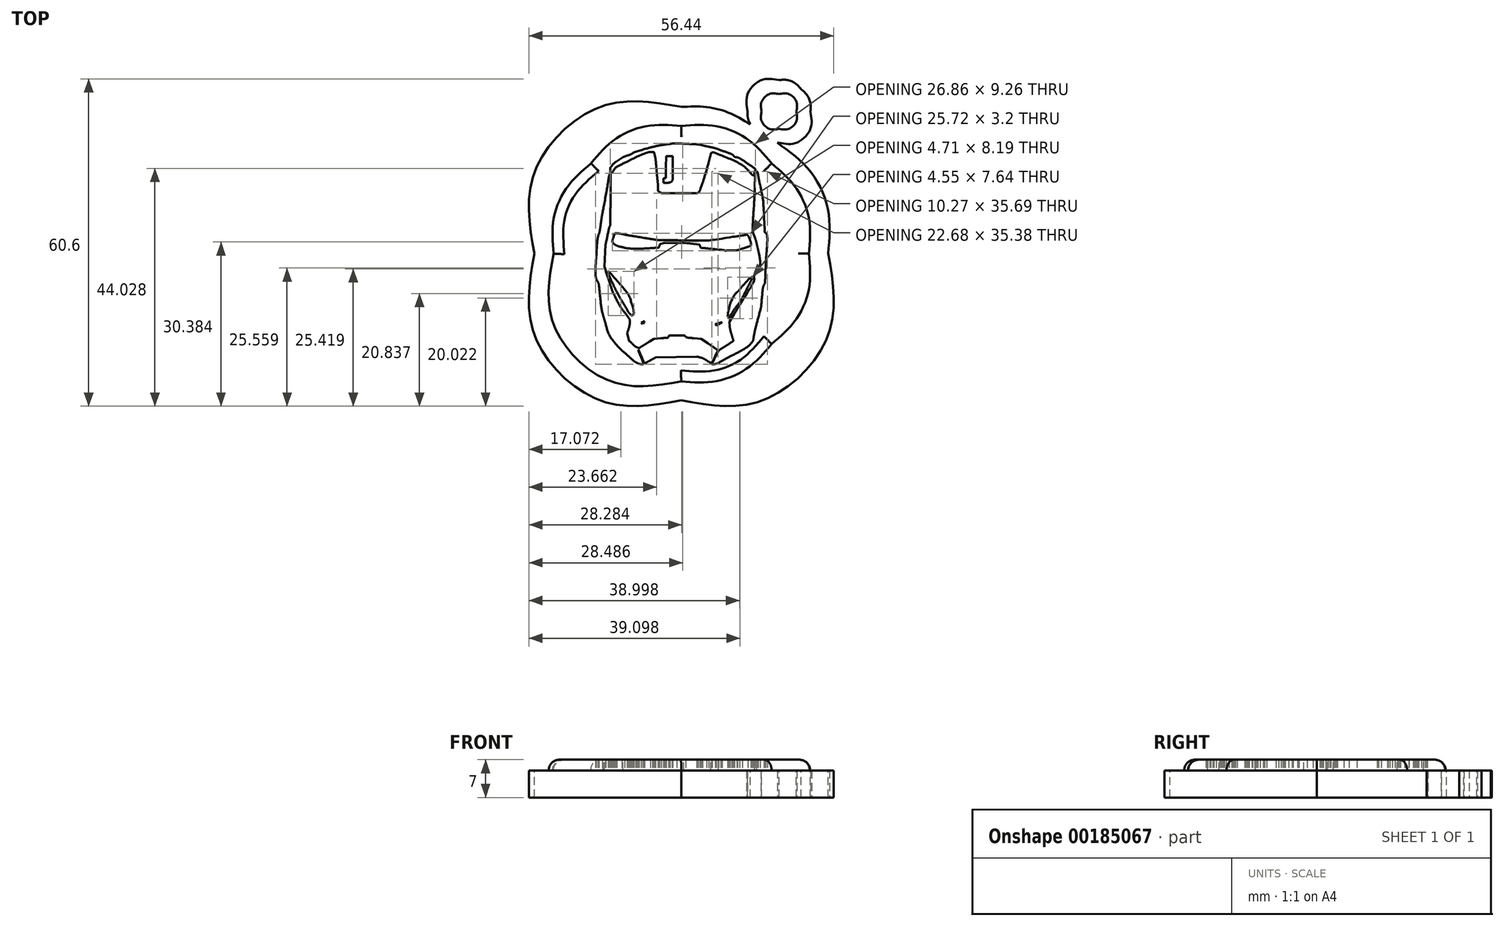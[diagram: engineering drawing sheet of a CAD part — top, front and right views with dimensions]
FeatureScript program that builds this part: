
annotation { "Feature Type Name" : "Feature", "Feature Type Description" : "" }
export const myFeature = defineFeature(function(context is Context, id is Id, definition is map)
    precondition{}
    {
        {
            var Q0;
            Q0=qCreatedBy(makeId("Top.planeOp"),FACE);
            var sketch = newSketch(context, id + "F0", { "sketchPlane" : qUnion([Q0])});
            skFitSpline(sketch, "E0", {"points": [v(-8.22, -22.7) * mm, v(-8.43, -22.6) * mm, v(-8.77, -22.38) * mm, v(-8.96, -22.21) * mm]});
            skFitSpline(sketch, "E1", {"points": [v(-8.96, -22.21) * mm, v(-9.15, -22.04) * mm, v(-9.54, -21.69) * mm, v(-9.83, -21.43) * mm]});
            skFitSpline(sketch, "E2", {"points": [v(-9.83, -21.43) * mm, v(-10.12, -21.17) * mm, v(-10.56, -20.8) * mm, v(-10.8, -20.6) * mm]});
            skFitSpline(sketch, "E3", {"points": [v(-10.8, -20.6) * mm, v(-11.06, -20.39) * mm, v(-11.61, -19.8) * mm, v(-12.04, -19.27) * mm]});
            skFitSpline(sketch, "E4", {"points": [v(-12.04, -19.27) * mm, v(-12.95, -18.16) * mm, v(-13.6, -16.93) * mm, v(-14, -15.53) * mm]});
            skFitSpline(sketch, "E5", {"points": [v(-14, -15.53) * mm, v(-14.14, -15.02) * mm, v(-14.36, -14.26) * mm, v(-14.48, -13.85) * mm]});
            skFitSpline(sketch, "E6", {"points": [v(-14.48, -13.85) * mm, v(-14.7, -13.05) * mm, v(-14.91, -11.53) * mm, v(-15.21, -8.5) * mm]});
            skFitSpline(sketch, "E7", {"points": [v(-15.21, -8.5) * mm, v(-15.23, -8.29) * mm, v(-15.34, -7.94) * mm, v(-15.45, -7.72) * mm]});
            skFitSpline(sketch, "E8", {"points": [v(-15.45, -7.72) * mm, v(-15.78, -7.08) * mm, v(-15.89, -5.4) * mm, v(-15.75, -3.2) * mm]});
            skFitSpline(sketch, "E9", {"points": [v(-15.75, -3.2) * mm, v(-15.59, -0.63) * mm, v(-15.46, 0.49) * mm, v(-15.26, 1.13) * mm]});
            skFitSpline(sketch, "E10", {"points": [v(-15.26, 1.13) * mm, v(-15.16, 1.44) * mm, v(-15, 2.32) * mm, v(-14.9, 3.1) * mm]});
            skFitSpline(sketch, "E11", {"points": [v(-14.9, 3.1) * mm, v(-14.79, 3.87) * mm, v(-14.66, 4.7) * mm, v(-14.6, 4.97) * mm]});
            skFitSpline(sketch, "E12", {"points": [v(-14.6, 4.97) * mm, v(-14.26, 6.74) * mm, v(-13.74, 9.57) * mm, v(-13.58, 10.63) * mm]});
            skFitSpline(sketch, "E13", {"points": [v(-13.58, 10.63) * mm, v(-13.47, 11.32) * mm, v(-13.35, 11.95) * mm, v(-13.32, 12.02) * mm]});
            skFitSpline(sketch, "E14", {"points": [v(-13.32, 12.02) * mm, v(-13.1, 12.44) * mm, v(-13.07, 11.84) * mm, v(-13.1, 7.5) * mm]});
            skFitSpline(sketch, "E15", {"points": [v(-13.1, 7.5) * mm, v(-13.12, 3.82) * mm, v(-13.16, 2.84) * mm, v(-13.27, 2.54) * mm]});
            skFitSpline(sketch, "E16", {"points": [v(-13.27, 2.54) * mm, v(-13.34, 2.33) * mm, v(-13.67, 0.81) * mm, v(-14, -0.83) * mm]});
            skFitSpline(sketch, "E17", {"points": [v(-14.24, -4.9) * mm, v(-14.04, -5.5) * mm, v(-13.61, -6.79) * mm, v(-13.3, -7.76) * mm]});
            skFitSpline(sketch, "E18", {"points": [v(-13.3, -7.76) * mm, v(-12.98, -8.74) * mm, v(-12.6, -9.77) * mm, v(-12.46, -10.06) * mm]});
            skFitSpline(sketch, "E19", {"points": [v(-12.46, -10.06) * mm, v(-11.7, -11.55) * mm, v(-11.06, -12.63) * mm, v(-10.45, -13.43) * mm]});
            skFitSpline(sketch, "E20", {"points": [v(-10.45, -13.43) * mm, v(-10.08, -13.92) * mm, v(-9.73, -14.4) * mm, v(-9.68, -14.5) * mm]});
            skFitSpline(sketch, "E21", {"points": [v(-9.68, -14.5) * mm, v(-9.52, -14.81) * mm, v(-9.71, -16.27) * mm, v(-10.03, -17.2) * mm]});
            skLineSegment(sketch, "E22", {"start": v(-14, -0.83) * mm, "end": v(-14.6, -3.82) * mm});
            skLineSegment(sketch, "E23", {"start": v(-14.6, -3.82) * mm, "end": v(-14.24, -4.9) * mm});
            skLineSegment(sketch, "E24", {"start": v(-14.24, -4.9) * mm, "end": v(-14, -0.83) * mm});
            skFitSpline(sketch, "E25", {"points": [v(-9.63, -18.65) * mm, v(-9.26, -19) * mm, v(-8.73, -19.48) * mm, v(-8.47, -19.74) * mm]});
            skLineSegment(sketch, "E26", {"start": v(-10.03, -17.2) * mm, "end": v(-10.32, -18.03) * mm});
            skLineSegment(sketch, "E27", {"start": v(-10.32, -18.03) * mm, "end": v(-9.63, -18.65) * mm});
            skLineSegment(sketch, "E28", {"start": v(-9.63, -18.65) * mm, "end": v(-10.03, -17.2) * mm});
            skFitSpline(sketch, "E29", {"points": [v(-7.78, -20) * mm, v(-7.66, -19.89) * mm, v(-7.37, -19.68) * mm, v(-7.13, -19.54) * mm]});
            skFitSpline(sketch, "E30", {"points": [v(-7.13, -19.54) * mm, v(-6.9, -19.4) * mm, v(-6.34, -19.06) * mm, v(-5.9, -18.78) * mm]});
            skLineSegment(sketch, "E31", {"start": v(-8.47, -19.74) * mm, "end": v(-8, -20.21) * mm});
            skLineSegment(sketch, "E32", {"start": v(-8, -20.21) * mm, "end": v(-7.78, -20) * mm});
            skLineSegment(sketch, "E33", {"start": v(-7.78, -20) * mm, "end": v(-8.47, -19.74) * mm});
            skFitSpline(sketch, "E34", {"points": [v(-3.8, -18.16) * mm, v(-2.63, -18.07) * mm, v(-2.5, -18.04) * mm, v(-2.37, -17.85) * mm]});
            skFitSpline(sketch, "E35", {"points": [v(-2.37, -17.85) * mm, v(-2.24, -17.65) * mm, v(-2.17, -17.64) * mm, v(-0.82, -17.64) * mm]});
            skFitSpline(sketch, "E36", {"points": [v(-0.82, -17.64) * mm, v(0.48, -17.64) * mm, v(0.6, -17.66) * mm, v(0.8, -17.84) * mm]});
            skFitSpline(sketch, "E37", {"points": [v(0.8, -17.84) * mm, v(0.97, -18) * mm, v(1.21, -18.05) * mm, v(2.35, -18.14) * mm]});
            skLineSegment(sketch, "E38", {"start": v(-5.9, -18.78) * mm, "end": v(-5.11, -18.26) * mm});
            skLineSegment(sketch, "E39", {"start": v(-5.11, -18.26) * mm, "end": v(-3.8, -18.16) * mm});
            skLineSegment(sketch, "E40", {"start": v(-3.8, -18.16) * mm, "end": v(-5.9, -18.78) * mm});
            skFitSpline(sketch, "E41", {"points": [v(4.95, -19.12) * mm, v(5.65, -19.59) * mm, v(6.34, -20.08) * mm, v(6.5, -20.2) * mm]});
            skLineSegment(sketch, "E42", {"start": v(2.35, -18.14) * mm, "end": v(3.7, -18.26) * mm});
            skLineSegment(sketch, "E43", {"start": v(3.7, -18.26) * mm, "end": v(4.95, -19.12) * mm});
            skLineSegment(sketch, "E44", {"start": v(4.95, -19.12) * mm, "end": v(2.35, -18.14) * mm});
            skFitSpline(sketch, "E45", {"points": [v(6.24, -21.52) * mm, v(5.94, -22.12) * mm, v(5.63, -22.63) * mm, v(5.56, -22.66) * mm]});
            skFitSpline(sketch, "E46", {"points": [v(5.56, -22.66) * mm, v(5.49, -22.7) * mm, v(5.1, -22.51) * mm, v(4.7, -22.27) * mm]});
            skFitSpline(sketch, "E47", {"points": [v(4.7, -22.27) * mm, v(4.13, -21.93) * mm, v(3.73, -21.77) * mm, v(2.85, -21.55) * mm]});
            skLineSegment(sketch, "E48", {"start": v(6.5, -20.2) * mm, "end": v(6.78, -20.43) * mm});
            skLineSegment(sketch, "E49", {"start": v(6.78, -20.43) * mm, "end": v(6.24, -21.52) * mm});
            skLineSegment(sketch, "E50", {"start": v(6.24, -21.52) * mm, "end": v(6.5, -20.2) * mm});
            skFitSpline(sketch, "E51", {"points": [v(-4.73, -21.7) * mm, v(-5.04, -21.87) * mm, v(-5.61, -22.18) * mm, v(-6, -22.4) * mm]});
            skFitSpline(sketch, "E52", {"points": [v(-6, -22.4) * mm, v(-6.38, -22.6) * mm, v(-6.74, -22.75) * mm, v(-6.8, -22.71) * mm]});
            skFitSpline(sketch, "E53", {"points": [v(-6.8, -22.71) * mm, v(-6.85, -22.68) * mm, v(-7, -22.42) * mm, v(-7.11, -22.13) * mm]});
            skFitSpline(sketch, "E54", {"points": [v(-7.11, -22.13) * mm, v(-7.53, -21.14) * mm, v(-7.9, -20.35) * mm, v(-7.93, -20.39) * mm]});
            skFitSpline(sketch, "E55", {"points": [v(-7.93, -20.39) * mm, v(-7.95, -20.4) * mm, v(-7.76, -20.94) * mm, v(-7.5, -21.57) * mm]});
            skFitSpline(sketch, "E56", {"points": [v(-7.5, -21.57) * mm, v(-7.24, -22.2) * mm, v(-7.03, -22.76) * mm, v(-7.03, -22.8) * mm]});
            skFitSpline(sketch, "E57", {"points": [v(-7.03, -22.8) * mm, v(-7.03, -22.95) * mm, v(-7.81, -22.88) * mm, v(-8.22, -22.7) * mm]});
            skLineSegment(sketch, "E58", {"start": v(2.85, -21.55) * mm, "end": v(1.73, -21.27) * mm});
            skLineSegment(sketch, "E59", {"start": v(1.73, -21.27) * mm, "end": v(-1.22, -21.34) * mm});
            skLineSegment(sketch, "E60", {"start": v(-1.22, -21.34) * mm, "end": v(-4.17, -21.4) * mm});
            skLineSegment(sketch, "E61", {"start": v(-4.17, -21.4) * mm, "end": v(-4.73, -21.7) * mm});
            skLineSegment(sketch, "E62", {"start": v(-4.73, -21.7) * mm, "end": v(2.85, -21.55) * mm});
            skFitSpline(sketch, "E63", {"points": [v(5.72, -22.81) * mm, v(5.88, -22.45) * mm, v(6.87, -20.56) * mm, v(6.95, -20.44) * mm]});
            skFitSpline(sketch, "E64", {"points": [v(6.95, -20.44) * mm, v(7.01, -20.37) * mm, v(7.59, -19.97) * mm, v(8.23, -19.56) * mm]});
            skFitSpline(sketch, "E65", {"points": [v(8.23, -19.56) * mm, v(8.87, -19.16) * mm, v(9.46, -18.77) * mm, v(9.52, -18.71) * mm]});
            skFitSpline(sketch, "E66", {"points": [v(9.52, -18.71) * mm, v(9.63, -18.62) * mm, v(9.6, -18.41) * mm, v(9.33, -17.54) * mm]});
            skFitSpline(sketch, "E67", {"points": [v(9.33, -17.54) * mm, v(9.15, -16.95) * mm, v(8.98, -16.17) * mm, v(8.95, -15.8) * mm]});
            skFitSpline(sketch, "E68", {"points": [v(9.78, -13.67) * mm, v(10.27, -12.85) * mm, v(11, -11.68) * mm, v(11.39, -11.05) * mm]});
            skFitSpline(sketch, "E69", {"points": [v(11.39, -11.05) * mm, v(12.53, -9.23) * mm, v(13.47, -7.38) * mm, v(13.47, -6.95) * mm]});
            skFitSpline(sketch, "E70", {"points": [v(13.47, -6.95) * mm, v(13.47, -6.67) * mm, v(13.61, -6.33) * mm, v(14.03, -5.57) * mm]});
            skFitSpline(sketch, "E71", {"points": [v(14.03, -5.57) * mm, v(14.42, -4.87) * mm, v(14.6, -4.46) * mm, v(14.6, -4.23) * mm]});
            skFitSpline(sketch, "E72", {"points": [v(14.6, -4.23) * mm, v(14.6, -3.9) * mm, v(14.38, -2.52) * mm, v(14.23, -1.87) * mm]});
            skFitSpline(sketch, "E73", {"points": [v(14.23, -1.87) * mm, v(14.18, -1.66) * mm, v(14.07, -1.18) * mm, v(13.98, -0.8) * mm]});
            skFitSpline(sketch, "E74", {"points": [v(13.98, -0.8) * mm, v(13.9, -0.4) * mm, v(13.72, 0.2) * mm, v(13.6, 0.57) * mm]});
            skFitSpline(sketch, "E75", {"points": [v(13.6, 0.57) * mm, v(13.27, 1.49) * mm, v(13.23, 2.84) * mm, v(13.43, 6.28) * mm]});
            skFitSpline(sketch, "E76", {"points": [v(13.43, 6.28) * mm, v(13.52, 7.82) * mm, v(13.6, 9.76) * mm, v(13.62, 10.58) * mm]});
            skFitSpline(sketch, "E77", {"points": [v(13.62, 10.58) * mm, v(13.64, 12.14) * mm, v(13.72, 12.62) * mm, v(13.95, 12.67) * mm]});
            skFitSpline(sketch, "E78", {"points": [v(13.95, 12.67) * mm, v(14.06, 12.69) * mm, v(14.2, 12.19) * mm, v(14.58, 10.23) * mm]});
            skFitSpline(sketch, "E79", {"points": [v(14.58, 10.23) * mm, v(15.08, 7.68) * mm, v(15.18, 6.84) * mm, v(15.35, 3.47) * mm]});
            skFitSpline(sketch, "E80", {"points": [v(15.35, 3.47) * mm, v(15.43, 1.84) * mm, v(15.47, 1.48) * mm, v(15.6, 1.33) * mm]});
            skFitSpline(sketch, "E81", {"points": [v(15.6, 1.33) * mm, v(15.82, 1.1) * mm, v(15.87, -0.9) * mm, v(15.72, -3) * mm]});
            skFitSpline(sketch, "E82", {"points": [v(15.72, -3) * mm, v(15.66, -3.81) * mm, v(15.6, -5.25) * mm, v(15.56, -6.17) * mm]});
            skFitSpline(sketch, "E83", {"points": [v(15.56, -6.17) * mm, v(15.51, -7.63) * mm, v(15.48, -7.91) * mm, v(15.3, -8.32) * mm]});
            skFitSpline(sketch, "E84", {"points": [v(15.3, -8.32) * mm, v(15.14, -8.69) * mm, v(15.05, -9.2) * mm, v(14.93, -10.53) * mm]});
            skFitSpline(sketch, "E85", {"points": [v(14.93, -10.53) * mm, v(14.77, -12.27) * mm, v(14.72, -12.52) * mm, v(14.27, -14.22) * mm]});
            skFitSpline(sketch, "E86", {"points": [v(14.27, -14.22) * mm, v(13.86, -15.73) * mm, v(13.58, -16.96) * mm, v(13.37, -18.1) * mm]});
            skFitSpline(sketch, "E87", {"points": [v(13.37, -18.1) * mm, v(13.29, -18.53) * mm, v(13.18, -18.79) * mm, v(12.98, -19.01) * mm]});
            skFitSpline(sketch, "E88", {"points": [v(12.98, -19.01) * mm, v(12.59, -19.46) * mm, v(11.16, -20.41) * mm, v(9.85, -21.1) * mm]});
            skFitSpline(sketch, "E89", {"points": [v(9.85, -21.1) * mm, v(9.24, -21.43) * mm, v(8.4, -21.87) * mm, v(8, -22.09) * mm]});
            skFitSpline(sketch, "E90", {"points": [v(8, -22.09) * mm, v(7.59, -22.3) * mm, v(7.08, -22.58) * mm, v(6.88, -22.69) * mm]});
            skFitSpline(sketch, "E91", {"points": [v(6.88, -22.69) * mm, v(6.52, -22.87) * mm, v(5.65, -22.97) * mm, v(5.72, -22.81) * mm]});
            skLineSegment(sketch, "E92", {"start": v(8.95, -15.8) * mm, "end": v(8.89, -15.14) * mm});
            skLineSegment(sketch, "E93", {"start": v(8.89, -15.14) * mm, "end": v(9.78, -13.67) * mm});
            skLineSegment(sketch, "E94", {"start": v(9.78, -13.67) * mm, "end": v(8.95, -15.8) * mm});
            skFitSpline(sketch, "E95", {"points": [v(5.7, -16.17) * mm, v(5.41, -15.87) * mm, v(5.07, -15.49) * mm, v(4.93, -15.31) * mm]});
            skFitSpline(sketch, "E96", {"points": [v(4.93, -15.31) * mm, v(4.77, -15.12) * mm, v(4.53, -14.96) * mm, v(4.32, -14.91) * mm]});
            skFitSpline(sketch, "E97", {"points": [v(4.32, -14.91) * mm, v(3.86, -14.8) * mm, v(-4.6, -14.64) * mm, v(-5.04, -14.74) * mm]});
            skFitSpline(sketch, "E98", {"points": [v(-5.04, -14.74) * mm, v(-5.31, -14.8) * mm, v(-5.55, -15) * mm, v(-6.17, -15.67) * mm]});
            skFitSpline(sketch, "E99", {"points": [v(-6.17, -15.67) * mm, v(-6.6, -16.14) * mm, v(-7.02, -16.52) * mm, v(-7.1, -16.52) * mm]});
            skFitSpline(sketch, "E100", {"points": [v(-7.1, -16.52) * mm, v(-7.2, -16.52) * mm, v(-7.6, -16.24) * mm, v(-8.01, -15.9) * mm]});
            skFitSpline(sketch, "E101", {"points": [v(-8.01, -15.9) * mm, v(-9.43, -14.71) * mm, v(-9.39, -14.76) * mm, v(-9.32, -14.45) * mm]});
            skFitSpline(sketch, "E102", {"points": [v(-9.32, -14.45) * mm, v(-9.28, -14.3) * mm, v(-9.2, -14.14) * mm, v(-9.12, -14.11) * mm]});
            skFitSpline(sketch, "E103", {"points": [v(-9.12, -14.11) * mm, v(-9.05, -14.08) * mm, v(-8.72, -14.28) * mm, v(-8.36, -14.57) * mm]});
            skFitSpline(sketch, "E104", {"points": [v(-8.36, -14.57) * mm, v(-8.01, -14.85) * mm, v(-7.6, -15.17) * mm, v(-7.43, -15.28) * mm]});
            skFitSpline(sketch, "E105", {"points": [v(-6.77, -15) * mm, v(-6.57, -14.73) * mm, v(-6.34, -14.39) * mm, v(-6.25, -14.25) * mm]});
            skFitSpline(sketch, "E106", {"points": [v(-6.25, -14.25) * mm, v(-5.88, -13.66) * mm, v(-6.02, -13.68) * mm, v(-1.47, -13.7) * mm]});
            skFitSpline(sketch, "E107", {"points": [v(-1.47, -13.7) * mm, v(2.96, -13.7) * mm, v(4.58, -13.76) * mm, v(4.95, -13.9) * mm]});
            skFitSpline(sketch, "E108", {"points": [v(4.95, -13.9) * mm, v(5.08, -13.96) * mm, v(5.39, -14.28) * mm, v(5.63, -14.63) * mm]});
            skFitSpline(sketch, "E109", {"points": [v(5.63, -14.63) * mm, v(5.88, -14.97) * mm, v(6.17, -15.37) * mm, v(6.29, -15.51) * mm]});
            skLineSegment(sketch, "E110", {"start": v(-7.43, -15.28) * mm, "end": v(-7.13, -15.5) * mm});
            skLineSegment(sketch, "E111", {"start": v(-7.13, -15.5) * mm, "end": v(-6.77, -15) * mm});
            skLineSegment(sketch, "E112", {"start": v(-6.77, -15) * mm, "end": v(-7.43, -15.28) * mm});
            skFitSpline(sketch, "E113", {"points": [v(7.53, -15.16) * mm, v(8.1, -14.83) * mm, v(8.61, -14.55) * mm, v(8.68, -14.55) * mm]});
            skFitSpline(sketch, "E114", {"points": [v(8.68, -14.55) * mm, v(8.76, -14.55) * mm, v(8.8, -14.65) * mm, v(8.78, -14.85) * mm]});
            skFitSpline(sketch, "E115", {"points": [v(8.78, -14.85) * mm, v(8.75, -15.1) * mm, v(8.62, -15.23) * mm, v(7.63, -15.92) * mm]});
            skFitSpline(sketch, "E116", {"points": [v(7.63, -15.92) * mm, v(7.01, -16.35) * mm, v(6.44, -16.7) * mm, v(6.35, -16.7) * mm]});
            skFitSpline(sketch, "E117", {"points": [v(6.35, -16.7) * mm, v(6.27, -16.7) * mm, v(5.97, -16.46) * mm, v(5.7, -16.17) * mm]});
            skLineSegment(sketch, "E118", {"start": v(6.29, -15.51) * mm, "end": v(6.5, -15.77) * mm});
            skLineSegment(sketch, "E119", {"start": v(6.5, -15.77) * mm, "end": v(7.53, -15.16) * mm});
            skLineSegment(sketch, "E120", {"start": v(7.53, -15.16) * mm, "end": v(6.29, -15.51) * mm});
            skFitSpline(sketch, "E121", {"points": [v(8.72, -14.34) * mm, v(8.62, -14.21) * mm, v(8.72, -13.1) * mm, v(8.9, -12.4) * mm]});
            skFitSpline(sketch, "E122", {"points": [v(8.9, -12.4) * mm, v(9.1, -11.62) * mm, v(10.02, -9.88) * mm, v(10.42, -9.54) * mm]});
            skFitSpline(sketch, "E123", {"points": [v(10.42, -9.54) * mm, v(10.48, -9.5) * mm, v(10.65, -9.3) * mm, v(10.8, -9.12) * mm]});
            skFitSpline(sketch, "E124", {"points": [v(10.8, -9.12) * mm, v(11.44, -8.33) * mm, v(12.94, -6.87) * mm, v(13.06, -6.91) * mm]});
            skFitSpline(sketch, "E125", {"points": [v(13.06, -6.91) * mm, v(13.15, -6.95) * mm, v(13.03, -7.25) * mm, v(12.62, -8.06) * mm]});
            skFitSpline(sketch, "E126", {"points": [v(12.62, -8.06) * mm, v(11.48, -10.26) * mm, v(10.72, -11.61) * mm, v(10.34, -12.12) * mm]});
            skFitSpline(sketch, "E127", {"points": [v(10.34, -12.12) * mm, v(9.88, -12.72) * mm, v(8.98, -14.2) * mm, v(8.98, -14.35) * mm]});
            skFitSpline(sketch, "E128", {"points": [v(8.98, -14.35) * mm, v(8.98, -14.5) * mm, v(8.84, -14.49) * mm, v(8.72, -14.34) * mm]});
            skFitSpline(sketch, "E129", {"points": [v(-9.47, -13.68) * mm, v(-9.64, -13.5) * mm, v(-9.87, -13.2) * mm, v(-9.97, -13) * mm]});
            skFitSpline(sketch, "E130", {"points": [v(-9.97, -13) * mm, v(-10.07, -12.8) * mm, v(-10.53, -12) * mm, v(-11, -11.23) * mm]});
            skFitSpline(sketch, "E131", {"points": [v(-11, -11.23) * mm, v(-11.46, -10.46) * mm, v(-12.05, -9.36) * mm, v(-12.33, -8.8) * mm]});
            skFitSpline(sketch, "E132", {"points": [v(-12.33, -8.8) * mm, v(-12.83, -7.74) * mm, v(-13.49, -6.17) * mm, v(-13.49, -6.01) * mm]});
            skFitSpline(sketch, "E133", {"points": [v(-13.49, -6.01) * mm, v(-13.49, -5.78) * mm, v(-13.14, -6.08) * mm, v(-12.3, -7.06) * mm]});
            skFitSpline(sketch, "E134", {"points": [v(-12.3, -7.06) * mm, v(-10.33, -9.34) * mm, v(-9.62, -10.41) * mm, v(-9.18, -11.74) * mm]});
            skFitSpline(sketch, "E135", {"points": [v(-9.18, -11.74) * mm, v(-8.92, -12.56) * mm, v(-8.82, -13.72) * mm, v(-9.01, -13.87) * mm]});
            skFitSpline(sketch, "E136", {"points": [v(-9.01, -13.87) * mm, v(-9.13, -13.97) * mm, v(-9.2, -13.93) * mm, v(-9.47, -13.68) * mm]});
            skFitSpline(sketch, "E137", {"points": [v(7.95, -1.88) * mm, v(7.92, -1.86) * mm, v(7.02, -1.75) * mm, v(5.94, -1.64) * mm]});
            skFitSpline(sketch, "E138", {"points": [v(5.94, -1.64) * mm, v(3.79, -1.42) * mm, v(3.58, -1.35) * mm, v(3.41, -0.8) * mm]});
            skFitSpline(sketch, "E139", {"points": [v(0.42, -0.5) * mm, v(-1.18, -0.49) * mm, v(-2.8, -0.47) * mm, v(-3.18, -0.47) * mm]});
            skLineSegment(sketch, "E140", {"start": v(3.41, -0.8) * mm, "end": v(3.32, -0.51) * mm});
            skLineSegment(sketch, "E141", {"start": v(3.32, -0.51) * mm, "end": v(0.42, -0.5) * mm});
            skLineSegment(sketch, "E142", {"start": v(0.42, -0.5) * mm, "end": v(3.41, -0.8) * mm});
            skFitSpline(sketch, "E143", {"points": [v(-3.98, -0.76) * mm, v(-4.17, -1.33) * mm, v(-4.27, -1.37) * mm, v(-5.73, -1.46) * mm]});
            skFitSpline(sketch, "E144", {"points": [v(-5.73, -1.46) * mm, v(-7.53, -1.57) * mm, v(-10.06, -1.47) * mm, v(-10.98, -1.26) * mm]});
            skFitSpline(sketch, "E145", {"points": [v(-10.98, -1.26) * mm, v(-11.64, -1.11) * mm, v(-12.47, -0.7) * mm, v(-12.72, -0.39) * mm]});
            skFitSpline(sketch, "E146", {"points": [v(-12.72, -0.39) * mm, v(-12.79, -0.3) * mm, v(-12.74, -0.04) * mm, v(-12.57, 0.5) * mm]});
            skLineSegment(sketch, "E147", {"start": v(-3.18, -0.47) * mm, "end": v(-3.87, -0.46) * mm});
            skLineSegment(sketch, "E148", {"start": v(-3.87, -0.46) * mm, "end": v(-3.98, -0.76) * mm});
            skLineSegment(sketch, "E149", {"start": v(-3.98, -0.76) * mm, "end": v(-3.18, -0.47) * mm});
            skFitSpline(sketch, "E150", {"points": [v(-11.92, 1.27) * mm, v(-11.7, 1.27) * mm, v(-11.13, 1.19) * mm, v(-10.65, 1.09) * mm]});
            skFitSpline(sketch, "E151", {"points": [v(-10.65, 1.09) * mm, v(-9.79, 0.9) * mm, v(-9.34, 0.83) * mm, v(-6.51, 0.38) * mm]});
            skFitSpline(sketch, "E152", {"points": [v(-6.51, 0.38) * mm, v(-5.69, 0.24) * mm, v(-4.9, 0.11) * mm, v(-4.78, 0.09) * mm]});
            skFitSpline(sketch, "E153", {"points": [v(-4.78, 0.09) * mm, v(-4.65, 0.06) * mm, v(-2.78, 0.02) * mm, v(-0.63, -0.01) * mm]});
            skFitSpline(sketch, "E154", {"points": [v(-0.63, -0.01) * mm, v(3.84, -0.08) * mm, v(5.67, 0.04) * mm, v(9.5, 0.62) * mm]});
            skFitSpline(sketch, "E155", {"points": [v(9.5, 0.62) * mm, v(12, 1) * mm, v(12.17, 1.02) * mm, v(12.3, 0.88) * mm]});
            skFitSpline(sketch, "E156", {"points": [v(12.3, 0.88) * mm, v(12.41, 0.77) * mm, v(12.91, -0.62) * mm, v(12.91, -0.81) * mm]});
            skFitSpline(sketch, "E157", {"points": [v(12.91, -0.81) * mm, v(12.91, -0.93) * mm, v(12.19, -1.26) * mm, v(11.28, -1.57) * mm]});
            skFitSpline(sketch, "E158", {"points": [v(11.28, -1.57) * mm, v(10.55, -1.8) * mm, v(10.26, -1.86) * mm, v(9.21, -1.9) * mm]});
            skFitSpline(sketch, "E159", {"points": [v(9.21, -1.9) * mm, v(8.54, -1.91) * mm, v(7.98, -1.9) * mm, v(7.95, -1.88) * mm]});
            skLineSegment(sketch, "E160", {"start": v(-12.57, 0.5) * mm, "end": v(-12.32, 1.27) * mm});
            skLineSegment(sketch, "E161", {"start": v(-12.32, 1.27) * mm, "end": v(-11.92, 1.27) * mm});
            skLineSegment(sketch, "E162", {"start": v(-11.92, 1.27) * mm, "end": v(-12.57, 0.5) * mm});
            skFitSpline(sketch, "E163", {"points": [v(-3.66, 8.74) * mm, v(-3.73, 8.76) * mm, v(-3.91, 8.86) * mm, v(-4.05, 8.96) * mm]});
            skFitSpline(sketch, "E164", {"points": [v(-4.05, 8.96) * mm, v(-4.29, 9.13) * mm, v(-4.31, 9.2) * mm, v(-4.31, 9.7) * mm]});
            skFitSpline(sketch, "E165", {"points": [v(-4.31, 9.7) * mm, v(-4.31, 10.02) * mm, v(-4.35, 10.66) * mm, v(-4.4, 11.13) * mm]});
            skFitSpline(sketch, "E166", {"points": [v(-4.4, 11.13) * mm, v(-4.45, 11.6) * mm, v(-4.54, 12.51) * mm, v(-4.6, 13.16) * mm]});
            skFitSpline(sketch, "E167", {"points": [v(-4.6, 13.16) * mm, v(-4.72, 14.56) * mm, v(-4.85, 15.51) * mm, v(-4.97, 15.99) * mm]});
            skFitSpline(sketch, "E168", {"points": [v(-4.97, 15.99) * mm, v(-5.06, 16.3) * mm, v(-5.1, 16.34) * mm, v(-5.34, 16.34) * mm]});
            skFitSpline(sketch, "E169", {"points": [v(-5.34, 16.34) * mm, v(-5.88, 16.34) * mm, v(-8.3, 15.43) * mm, v(-9.97, 14.59) * mm]});
            skFitSpline(sketch, "E170", {"points": [v(-9.97, 14.59) * mm, v(-11.42, 13.87) * mm, v(-12.25, 13.33) * mm, v(-12.5, 12.96) * mm]});
            skFitSpline(sketch, "E171", {"points": [v(-12.5, 12.96) * mm, v(-12.85, 12.46) * mm, v(-13.08, 12.47) * mm, v(-13.13, 13) * mm]});
            skFitSpline(sketch, "E172", {"points": [v(-13.13, 13) * mm, v(-13.16, 13.34) * mm, v(-13.13, 13.44) * mm, v(-12.84, 13.8) * mm]});
            skFitSpline(sketch, "E173", {"points": [v(-12.84, 13.8) * mm, v(-12.46, 14.25) * mm, v(-10.5, 15.5) * mm, v(-9.78, 15.75) * mm]});
            skFitSpline(sketch, "E174", {"points": [v(-9.78, 15.75) * mm, v(-9.53, 15.83) * mm, v(-9.24, 15.95) * mm, v(-9.13, 16.02) * mm]});
            skFitSpline(sketch, "E175", {"points": [v(-9.13, 16.02) * mm, v(-8.86, 16.19) * mm, v(-6.54, 16.95) * mm, v(-5.32, 17.26) * mm]});
            skFitSpline(sketch, "E176", {"points": [v(-5.32, 17.26) * mm, v(-4.74, 17.42) * mm, v(-3.6, 17.63) * mm, v(-2.77, 17.74) * mm]});
            skFitSpline(sketch, "E177", {"points": [v(-2.77, 17.74) * mm, v(-1.37, 17.94) * mm, v(-1.12, 17.94) * mm, v(0.93, 17.85) * mm]});
            skFitSpline(sketch, "E178", {"points": [v(0.93, 17.85) * mm, v(2.5, 17.79) * mm, v(3.36, 17.7) * mm, v(3.93, 17.58) * mm]});
            skFitSpline(sketch, "E179", {"points": [v(3.93, 17.58) * mm, v(4.36, 17.47) * mm, v(5.06, 17.32) * mm, v(5.47, 17.23) * mm]});
            skFitSpline(sketch, "E180", {"points": [v(5.47, 17.23) * mm, v(5.88, 17.14) * mm, v(6.5, 16.97) * mm, v(6.83, 16.85) * mm]});
            skFitSpline(sketch, "E181", {"points": [v(6.83, 16.85) * mm, v(8.6, 16.21) * mm, v(9.51, 15.82) * mm, v(9.68, 15.63) * mm]});
            skFitSpline(sketch, "E182", {"points": [v(9.68, 15.63) * mm, v(9.8, 15.5) * mm, v(10.03, 15.4) * mm, v(10.26, 15.36) * mm]});
            skFitSpline(sketch, "E183", {"points": [v(10.26, 15.36) * mm, v(10.53, 15.31) * mm, v(11.01, 15.05) * mm, v(11.85, 14.48) * mm]});
            skFitSpline(sketch, "E184", {"points": [v(11.85, 14.48) * mm, v(13.28, 13.52) * mm, v(13.7, 13.13) * mm, v(13.62, 12.84) * mm]});
            skFitSpline(sketch, "E185", {"points": [v(13.62, 12.84) * mm, v(13.59, 12.73) * mm, v(13.54, 12.53) * mm, v(13.5, 12.38) * mm]});
            skFitSpline(sketch, "E186", {"points": [v(13.5, 12.38) * mm, v(13.42, 12.01) * mm, v(13.2, 12.06) * mm, v(12.72, 12.56) * mm]});
            skFitSpline(sketch, "E187", {"points": [v(12.72, 12.56) * mm, v(11.7, 13.6) * mm, v(9.84, 14.7) * mm, v(7.3, 15.74) * mm]});
            skFitSpline(sketch, "E188", {"points": [v(7.3, 15.74) * mm, v(6.23, 16.17) * mm, v(5.81, 16.3) * mm, v(5.7, 16.24) * mm]});
            skFitSpline(sketch, "E189", {"points": [v(5.7, 16.24) * mm, v(5.51, 16.14) * mm, v(5.45, 15.96) * mm, v(5.1, 14.56) * mm]});
            skFitSpline(sketch, "E190", {"points": [v(5.1, 14.56) * mm, v(4.86, 13.61) * mm, v(3.93, 10.6) * mm, v(3.53, 9.48) * mm]});
            skFitSpline(sketch, "E191", {"points": [v(3.53, 9.48) * mm, v(3.42, 9.17) * mm, v(3.25, 8.89) * mm, v(3.14, 8.82) * mm]});
            skFitSpline(sketch, "E192", {"points": [v(3.14, 8.82) * mm, v(3, 8.74) * mm, v(2.04, 8.7) * mm, v(-0.29, 8.7) * mm]});
            skFitSpline(sketch, "E193", {"points": [v(-0.29, 8.7) * mm, v(-2.06, 8.7) * mm, v(-3.58, 8.71) * mm, v(-3.66, 8.74) * mm]});
            skFitSpline(sketch, "E194", {"points": [v(-2.08, 10.73) * mm, v(-1.91, 10.79) * mm, v(-1.74, 10.91) * mm, v(-1.69, 11) * mm]});
            skFitSpline(sketch, "E195", {"points": [v(-1.69, 11) * mm, v(-1.64, 11.1) * mm, v(-1.6, 12.12) * mm, v(-1.6, 13.38) * mm]});
            skFitSpline(sketch, "E196", {"points": [v(-2.84, 13.55) * mm, v(-2.86, 11.52) * mm, v(-2.86, 11.52) * mm, v(-3.07, 11.49) * mm]});
            skFitSpline(sketch, "E197", {"points": [v(-3.07, 11.49) * mm, v(-3.25, 11.46) * mm, v(-3.28, 11.4) * mm, v(-3.28, 11.04) * mm]});
            skLineSegment(sketch, "E198", {"start": v(-1.6, 13.38) * mm, "end": v(-1.6, 15.59) * mm});
            skLineSegment(sketch, "E199", {"start": v(-1.6, 15.59) * mm, "end": v(-2.2, 15.59) * mm});
            skLineSegment(sketch, "E200", {"start": v(-2.2, 15.59) * mm, "end": v(-2.81, 15.59) * mm});
            skLineSegment(sketch, "E201", {"start": v(-2.81, 15.59) * mm, "end": v(-2.84, 13.55) * mm});
            skFitSpline(sketch, "E202", {"points": [v(-2.83, 10.63) * mm, v(-2.58, 10.63) * mm, v(-2.24, 10.68) * mm, v(-2.08, 10.73) * mm]});
            skLineSegment(sketch, "E203", {"start": v(-3.28, 11.04) * mm, "end": v(-3.28, 10.63) * mm});
            skLineSegment(sketch, "E204", {"start": v(-3.28, 10.63) * mm, "end": v(-2.83, 10.63) * mm});
            skFitSpline(sketch, "E205", {"points": [v(0.1, 12.3) * mm, v(0.11, 13.95) * mm, v(0.11, 13.95) * mm, v(0.23, 13.25) * mm]});
            skFitSpline(sketch, "E206", {"points": [v(0.23, 13.25) * mm, v(0.3, 12.86) * mm, v(0.4, 12.12) * mm, v(0.46, 11.59) * mm]});
            skFitSpline(sketch, "E207", {"points": [v(0.94, 10.63) * mm, v(1.14, 10.63) * mm, v(1.3, 10.66) * mm, v(1.3, 10.7) * mm]});
            skFitSpline(sketch, "E208", {"points": [v(1.3, 10.7) * mm, v(1.3, 10.87) * mm, v(1.69, 13.77) * mm, v(1.72, 13.86) * mm]});
            skFitSpline(sketch, "E209", {"points": [v(1.72, 13.86) * mm, v(1.74, 13.9) * mm, v(1.76, 13.36) * mm, v(1.77, 12.64) * mm]});
            skFitSpline(sketch, "E210", {"points": [v(1.77, 12.64) * mm, v(1.77, 11.92) * mm, v(1.8, 11.17) * mm, v(1.83, 10.98) * mm]});
            skLineSegment(sketch, "E211", {"start": v(0.46, 11.59) * mm, "end": v(0.58, 10.63) * mm});
            skLineSegment(sketch, "E212", {"start": v(0.58, 10.63) * mm, "end": v(0.94, 10.63) * mm});
            skFitSpline(sketch, "E213", {"points": [v(2.11, 15.59) * mm, v(1.2, 15.59) * mm, v(1.3, 15.71) * mm, v(1.11, 14.25) * mm]});
            skFitSpline(sketch, "E214", {"points": [v(1.11, 14.25) * mm, v(1.05, 13.74) * mm, v(0.97, 13.36) * mm, v(0.93, 13.4) * mm]});
            skFitSpline(sketch, "E215", {"points": [v(0.93, 13.4) * mm, v(0.9, 13.45) * mm, v(0.81, 13.86) * mm, v(0.75, 14.33) * mm]});
            skFitSpline(sketch, "E216", {"points": [v(0.75, 14.33) * mm, v(0.56, 15.71) * mm, v(0.65, 15.59) * mm, v(-0.25, 15.59) * mm]});
            skLineSegment(sketch, "E217", {"start": v(1.83, 10.98) * mm, "end": v(1.9, 10.63) * mm});
            skLineSegment(sketch, "E218", {"start": v(1.9, 10.63) * mm, "end": v(2.4, 10.63) * mm});
            skLineSegment(sketch, "E219", {"start": v(2.4, 10.63) * mm, "end": v(2.9, 10.63) * mm});
            skLineSegment(sketch, "E220", {"start": v(2.9, 10.63) * mm, "end": v(2.9, 13.1) * mm});
            skLineSegment(sketch, "E221", {"start": v(2.9, 13.1) * mm, "end": v(2.9, 15.59) * mm});
            skLineSegment(sketch, "E222", {"start": v(2.9, 15.59) * mm, "end": v(2.11, 15.59) * mm});
            skFitSpline(sketch, "E223", {"points": [v(23.65, -2.5) * mm, v(23.65, -8.76) * mm, v(21.15, -14.78) * mm, v(16.72, -19.21) * mm]});
            skFitSpline(sketch, "E224", {"points": [v(16.72, -19.21) * mm, v(12.29, -23.64) * mm, v(6.27, -26.14) * mm, v(0, -26.14) * mm]});
            skFitSpline(sketch, "E225", {"points": [v(0, -26.14) * mm, v(-13.06, -26.14) * mm, v(-23.65, -15.55) * mm, v(-23.65, -2.5) * mm]});
            skFitSpline(sketch, "E226", {"points": [v(-23.65, -2.5) * mm, v(-23.65, 3.78) * mm, v(-21.15, 9.8) * mm, v(-16.72, 14.23) * mm]});
            skFitSpline(sketch, "E227", {"points": [v(-16.72, 14.23) * mm, v(-12.29, 18.66) * mm, v(-6.27, 21.16) * mm, v(0, 21.16) * mm]});
            skFitSpline(sketch, "E228", {"points": [v(0, 21.16) * mm, v(6.27, 21.16) * mm, v(12.29, 18.66) * mm, v(16.72, 14.23) * mm]});
            skFitSpline(sketch, "E229", {"points": [v(16.72, 14.23) * mm, v(21.15, 9.8) * mm, v(23.65, 3.78) * mm, v(23.65, -2.5) * mm]});
            skLineSegment(sketch, "E230", {"start": v(-0.25, 15.59) * mm, "end": v(-1.04, 15.59) * mm});
            skLineSegment(sketch, "E231", {"start": v(-1.04, 15.59) * mm, "end": v(-1.04, 13.1) * mm});
            skLineSegment(sketch, "E232", {"start": v(-1.04, 13.1) * mm, "end": v(-1.04, 10.63) * mm});
            skLineSegment(sketch, "E233", {"start": v(-1.04, 10.63) * mm, "end": v(-0.47, 10.63) * mm});
            skLineSegment(sketch, "E234", {"start": v(-0.47, 10.63) * mm, "end": v(0.09, 10.63) * mm});
            skLineSegment(sketch, "E235", {"start": v(0.09, 10.63) * mm, "end": v(0.1, 12.3) * mm});
            skFitSpline(sketch, "E236", {"points": [v(18.08, 29.67) * mm, v(14.87, 29.67) * mm, v(12.26, 27.07) * mm, v(12.26, 23.85) * mm]});
            skFitSpline(sketch, "E237", {"points": [v(12.26, 23.85) * mm, v(12.27, 23.04) * mm, v(12.44, 22.23) * mm, v(12.78, 21.48) * mm]});
            skFitSpline(sketch, "E238", {"points": [v(12.78, 21.48) * mm, v(8.84, 23.58) * mm, v(4.46, 24.68) * mm, v(0, 24.69) * mm]});
            skFitSpline(sketch, "E239", {"points": [v(0, 24.69) * mm, v(-15.01, 24.69) * mm, v(-27.18, 12.52) * mm, v(-27.18, -2.5) * mm]});
            skFitSpline(sketch, "E240", {"points": [v(-27.18, -2.5) * mm, v(-27.18, -17.5) * mm, v(-15.01, -29.67) * mm, v(0, -29.67) * mm]});
            skFitSpline(sketch, "E241", {"points": [v(0, -29.67) * mm, v(15.01, -29.67) * mm, v(27.18, -17.5) * mm, v(27.18, -2.5) * mm]});
            skFitSpline(sketch, "E242", {"points": [v(27.18, -2.5) * mm, v(27.17, 5.4) * mm, v(23.74, 12.9) * mm, v(17.77, 18.05) * mm]});
            skFitSpline(sketch, "E243", {"points": [v(17.77, 18.05) * mm, v(17.87, 18.05) * mm, v(17.98, 18.04) * mm, v(18.08, 18.04) * mm]});
            skFitSpline(sketch, "E244", {"points": [v(18.08, 18.04) * mm, v(21.29, 18.04) * mm, v(23.9, 20.64) * mm, v(23.9, 23.85) * mm]});
            skFitSpline(sketch, "E245", {"points": [v(23.9, 23.85) * mm, v(23.9, 25.4) * mm, v(23.28, 26.88) * mm, v(22.2, 27.97) * mm]});
            skFitSpline(sketch, "E246", {"points": [v(22.2, 27.97) * mm, v(21.1, 29.06) * mm, v(19.62, 29.67) * mm, v(18.08, 29.67) * mm]});
            skFitSpline(sketch, "E247", {"points": [v(21.3, 23.85) * mm, v(21.3, 22.07) * mm, v(19.86, 20.63) * mm, v(18.08, 20.63) * mm]});
            skFitSpline(sketch, "E248", {"points": [v(18.08, 20.63) * mm, v(16.3, 20.63) * mm, v(14.85, 22.07) * mm, v(14.85, 23.85) * mm]});
            skFitSpline(sketch, "E249", {"points": [v(14.85, 23.85) * mm, v(14.85, 25.63) * mm, v(16.3, 27.08) * mm, v(18.08, 27.08) * mm]});
            skFitSpline(sketch, "E250", {"points": [v(18.08, 27.08) * mm, v(19.86, 27.08) * mm, v(21.3, 25.63) * mm, v(21.3, 23.85) * mm]});
            skSolve(sketch);
        }
        {
            var Q0;
            Q0=makeQuery(id+"F0.imprint","IMPRINT",FACE,{"disambiguationData":[TD([[makeQuery(id+"F0.imprint","IMPRINT",EDGE,{"derivedFrom":sQuery(id+"F0.wireOp",EDGE,"E0")}),1.0]])]});
            extrude(context, id + "F1", {"entities" : qUnion([Q0]), "depth" : 2 * mm});
        }
        {
            var Q0;
            Q0=makeQuery(id+"F0.imprint","IMPRINT",FACE,{"disambiguationData":[TD([[makeQuery(id+"F0.imprint","IMPRINT",EDGE,{"derivedFrom":sQuery(id+"F0.wireOp",EDGE,"E194")}),1.0]])]});
            var Q1;
            Q1=makeQuery(id+"F0.imprint","IMPRINT",FACE,{"disambiguationData":[TD([[makeQuery(id+"F0.imprint","IMPRINT",EDGE,{"derivedFrom":sQuery(id+"F0.wireOp",EDGE,"E205")}),1.0]])]});
            extrude(context, id + "F2", {"entities" : qUnion([Q0, Q1]), "depth" : 2 * mm});
        }
        {
            var Q0;
            Q0=makeQuery(id+"F1.opExtrude","CAP_EDGE",EDGE,{"disambiguationData":[OSD([sQuery(id+"F0.wireOp",EDGE,"E227")])],"isStart":false});
            var Q1;
            Q1=makeQuery(id+"F1.opExtrude","CAP_EDGE",EDGE,{"disambiguationData":[OSD([sQuery(id+"F0.wireOp",EDGE,"E228")])],"isStart":false});
            var Q2;
            Q2=makeQuery(id+"F1.opExtrude","CAP_EDGE",EDGE,{"disambiguationData":[OSD([sQuery(id+"F0.wireOp",EDGE,"E229")])],"isStart":false});
            var Q3;
            Q3=makeQuery(id+"F1.opExtrude","CAP_EDGE",EDGE,{"disambiguationData":[OSD([sQuery(id+"F0.wireOp",EDGE,"E223")])],"isStart":false});
            var Q4;
            Q4=makeQuery(id+"F1.opExtrude","CAP_EDGE",EDGE,{"disambiguationData":[OSD([sQuery(id+"F0.wireOp",EDGE,"E224")])],"isStart":false});
            var Q5;
            Q5=makeQuery(id+"F1.opExtrude","CAP_EDGE",EDGE,{"disambiguationData":[OSD([sQuery(id+"F0.wireOp",EDGE,"E225")])],"isStart":false});
            var Q6;
            Q6=makeQuery(id+"F1.opExtrude","CAP_EDGE",EDGE,{"disambiguationData":[OSD([sQuery(id+"F0.wireOp",EDGE,"E226")])],"isStart":false});
            fillet(context, id + "F3", {"entities" : qUnion([Q0, Q1, Q2, Q3, Q4, Q5, Q6]), "radius" : 2 * mm, "tangentPropagation" : true, "allowEdgeOverflow" : false});
        }
        {
            var Q0;
            Q0=makeQuery(id+"F0.imprint","IMPRINT",FACE,{"disambiguationData":[TD([[makeQuery(id+"F0.imprint","IMPRINT",EDGE,{"derivedFrom":sQuery(id+"F0.wireOp",EDGE,"E223")}),1.0]])]});
            var Q1;
            Q1=makeQuery(id+"F0.imprint","IMPRINT",FACE,{"disambiguationData":[TD([[makeQuery(id+"F0.imprint","IMPRINT",EDGE,{"derivedFrom":sQuery(id+"F0.wireOp",EDGE,"E0")}),1.0]])]});
            var Q2;
            Q2=makeQuery(id+"F0.imprint","IMPRINT",FACE,{"disambiguationData":[TD([[makeQuery(id+"F0.imprint","IMPRINT",EDGE,{"derivedFrom":sQuery(id+"F0.wireOp",EDGE,"E0")}),-1.0]])]});
            var Q3;
            Q3=makeQuery(id+"F0.imprint","IMPRINT",FACE,{"disambiguationData":[TD([[makeQuery(id+"F0.imprint","IMPRINT",EDGE,{"derivedFrom":sQuery(id+"F0.wireOp",EDGE,"E63")}),-1.0]])]});
            var Q4;
            Q4=makeQuery(id+"F0.imprint","IMPRINT",FACE,{"disambiguationData":[TD([[makeQuery(id+"F0.imprint","IMPRINT",EDGE,{"derivedFrom":sQuery(id+"F0.wireOp",EDGE,"E121")}),-1.0]])]});
            var Q5;
            Q5=makeQuery(id+"F0.imprint","IMPRINT",FACE,{"disambiguationData":[TD([[makeQuery(id+"F0.imprint","IMPRINT",EDGE,{"derivedFrom":sQuery(id+"F0.wireOp",EDGE,"E92")}),-1.0]])]});
            var Q6;
            Q6=makeQuery(id+"F0.imprint","IMPRINT",FACE,{"disambiguationData":[TD([[makeQuery(id+"F0.imprint","IMPRINT",EDGE,{"derivedFrom":sQuery(id+"F0.wireOp",EDGE,"E95")}),-1.0]])]});
            var Q7;
            Q7=makeQuery(id+"F0.imprint","IMPRINT",FACE,{"disambiguationData":[TD([[makeQuery(id+"F0.imprint","IMPRINT",EDGE,{"derivedFrom":sQuery(id+"F0.wireOp",EDGE,"E118")}),1.0]])]});
            var Q8;
            Q8=makeQuery(id+"F0.imprint","IMPRINT",FACE,{"disambiguationData":[TD([[makeQuery(id+"F0.imprint","IMPRINT",EDGE,{"derivedFrom":sQuery(id+"F0.wireOp",EDGE,"E48")}),-1.0]])]});
            var Q9;
            Q9=makeQuery(id+"F0.imprint","IMPRINT",FACE,{"disambiguationData":[TD([[makeQuery(id+"F0.imprint","IMPRINT",EDGE,{"derivedFrom":sQuery(id+"F0.wireOp",EDGE,"E42")}),-1.0]])]});
            var Q10;
            Q10=makeQuery(id+"F0.imprint","IMPRINT",FACE,{"disambiguationData":[TD([[makeQuery(id+"F0.imprint","IMPRINT",EDGE,{"derivedFrom":sQuery(id+"F0.wireOp",EDGE,"E58")}),1.0]])]});
            var Q11;
            Q11=makeQuery(id+"F0.imprint","IMPRINT",FACE,{"disambiguationData":[TD([[makeQuery(id+"F0.imprint","IMPRINT",EDGE,{"derivedFrom":sQuery(id+"F0.wireOp",EDGE,"E38")}),-1.0]])]});
            var Q12;
            Q12=makeQuery(id+"F0.imprint","IMPRINT",FACE,{"disambiguationData":[TD([[makeQuery(id+"F0.imprint","IMPRINT",EDGE,{"derivedFrom":sQuery(id+"F0.wireOp",EDGE,"E31")}),1.0]])]});
            var Q13;
            Q13=makeQuery(id+"F0.imprint","IMPRINT",FACE,{"disambiguationData":[TD([[makeQuery(id+"F0.imprint","IMPRINT",EDGE,{"derivedFrom":sQuery(id+"F0.wireOp",EDGE,"E26")}),1.0]])]});
            var Q14;
            Q14=makeQuery(id+"F0.imprint","IMPRINT",FACE,{"disambiguationData":[TD([[makeQuery(id+"F0.imprint","IMPRINT",EDGE,{"derivedFrom":sQuery(id+"F0.wireOp",EDGE,"E110")}),1.0]])]});
            var Q15;
            Q15=makeQuery(id+"F0.imprint","IMPRINT",FACE,{"disambiguationData":[TD([[makeQuery(id+"F0.imprint","IMPRINT",EDGE,{"derivedFrom":sQuery(id+"F0.wireOp",EDGE,"E129")}),-1.0]])]});
            var Q16;
            Q16=makeQuery(id+"F0.imprint","IMPRINT",FACE,{"disambiguationData":[TD([[makeQuery(id+"F0.imprint","IMPRINT",EDGE,{"derivedFrom":sQuery(id+"F0.wireOp",EDGE,"E137")}),-1.0]])]});
            var Q17;
            Q17=makeQuery(id+"F0.imprint","IMPRINT",FACE,{"disambiguationData":[TD([[makeQuery(id+"F0.imprint","IMPRINT",EDGE,{"derivedFrom":sQuery(id+"F0.wireOp",EDGE,"E160")}),-1.0]])]});
            var Q18;
            Q18=makeQuery(id+"F0.imprint","IMPRINT",FACE,{"disambiguationData":[TD([[makeQuery(id+"F0.imprint","IMPRINT",EDGE,{"derivedFrom":sQuery(id+"F0.wireOp",EDGE,"E22")}),1.0]])]});
            var Q19;
            Q19=makeQuery(id+"F0.imprint","IMPRINT",FACE,{"disambiguationData":[TD([[makeQuery(id+"F0.imprint","IMPRINT",EDGE,{"derivedFrom":sQuery(id+"F0.wireOp",EDGE,"E147")}),1.0]])]});
            var Q20;
            Q20=makeQuery(id+"F0.imprint","IMPRINT",FACE,{"disambiguationData":[TD([[makeQuery(id+"F0.imprint","IMPRINT",EDGE,{"derivedFrom":sQuery(id+"F0.wireOp",EDGE,"E140")}),1.0]])]});
            var Q21;
            Q21=makeQuery(id+"F0.imprint","IMPRINT",FACE,{"disambiguationData":[TD([[makeQuery(id+"F0.imprint","IMPRINT",EDGE,{"derivedFrom":sQuery(id+"F0.wireOp",EDGE,"E163")}),-1.0]])]});
            var Q22;
            Q22=makeQuery(id+"F0.imprint","IMPRINT",FACE,{"disambiguationData":[TD([[makeQuery(id+"F0.imprint","IMPRINT",EDGE,{"derivedFrom":sQuery(id+"F0.wireOp",EDGE,"E205")}),1.0]])]});
            var Q23;
            Q23=makeQuery(id+"F0.imprint","IMPRINT",FACE,{"disambiguationData":[TD([[makeQuery(id+"F0.imprint","IMPRINT",EDGE,{"derivedFrom":sQuery(id+"F0.wireOp",EDGE,"E194")}),1.0]])]});
            extrude(context, id + "F4", {"entities" : qUnion([Q0, Q1, Q2, Q3, Q4, Q5, Q6, Q7, Q8, Q9, Q10, Q11, Q12, Q13, Q14, Q15, Q16, Q17, Q18, Q19, Q20, Q21, Q22, Q23]), "oppositeDirection" : true, "depth" : 5 * mm});
        }
    });
